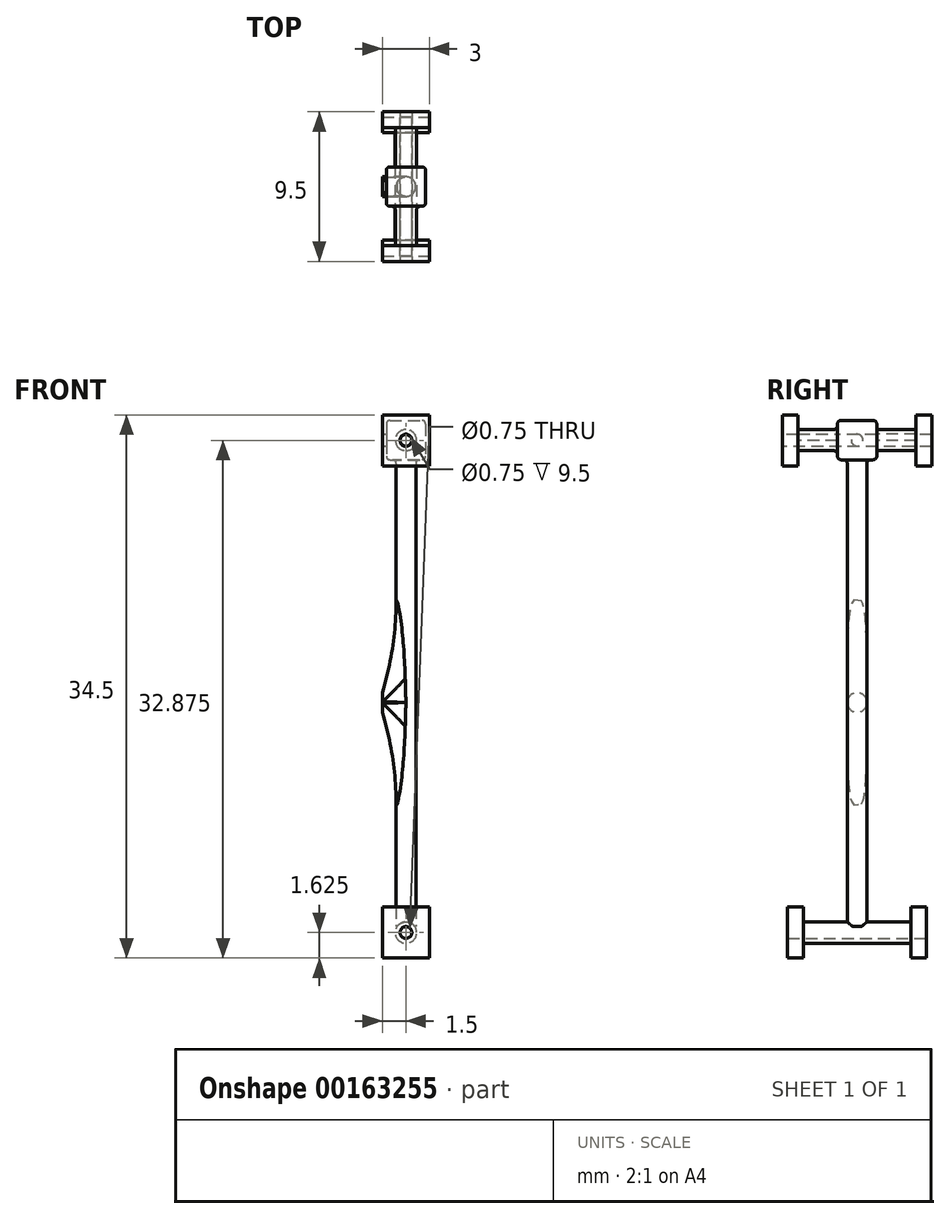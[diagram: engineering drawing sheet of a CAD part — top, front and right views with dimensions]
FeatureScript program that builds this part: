
annotation { "Feature Type Name" : "Feature", "Feature Type Description" : "" }
export const myFeature = defineFeature(function(context is Context, id is Id, definition is map)
    precondition{}
    {
        {
            var Q0;
            Q0=qCreatedBy(makeId("Front.planeOp"),FACE);
            var sketch = newSketch(context, id + "F0", { "sketchPlane" : qUnion([Q0])});
            skLineSegment(sketch, "E0.bottom", {"start": v(0, 0) * mm, "end": v(3, 0) * mm});
            skLineSegment(sketch, "E0.top", {"start": v(0, -3.25) * mm, "end": v(3, -3.25) * mm});
            skLineSegment(sketch, "E0.left", {"start": v(0, 0) * mm, "end": v(0, -3.25) * mm});
            skLineSegment(sketch, "E0.right", {"start": v(3, 0) * mm, "end": v(3, -3.25) * mm});
            skSolve(sketch);
        }
        {
            var Q0;
            Q0 = qSketchRegion(id + "F0", true);
            extrude(context, id + "F1", {"entities" : qUnion([Q0]), "depth" : 1 * mm});
        }
        {
            var Q0;
            Q0=makeQuery(id+"F1.opExtrude","CAP_FACE",FACE,{"disambiguationData":[OSD([sQuery(id+"F0.wireOp",EDGE,"E0.bottom"),sQuery(id+"F0.wireOp",EDGE,"E0.top"),sQuery(id+"F0.wireOp",EDGE,"E0.left"),sQuery(id+"F0.wireOp",EDGE,"E0.right")])],"isStart":true});
            var sketch = newSketch(context, id + "F2", { "sketchPlane" : qUnion([Q0])});
            skCircle(sketch, "E1", {"center": v(-1.5, -1.63) * mm, "radius": 0.38 * mm});
            skPoint(sketch, "E1.centerSnap0", {"position": v(0, -1.63) * mm});
            skPoint(sketch, "E1.centerSnap1", {"position": v(-1.5, 0) * mm});
            skSolve(sketch);
        }
        {
            var Q0;
            Q0 = qSketchRegion(id + "F2", true);
            extrude(context, id + "F3", {"entities" : qUnion([Q0]), "operationType" : NewBodyOperationType.REMOVE, "endBound" : BoundingType.THROUGH_ALL, "oppositeDirection" : true, "depth" : 25 * mm});
        }
        {
            var Q0;
            Q0=makeQuery(id+"F1.opExtrude","CAP_FACE",FACE,{"disambiguationData":[OSD([sQuery(id+"F0.wireOp",EDGE,"E0.bottom"),sQuery(id+"F0.wireOp",EDGE,"E0.top"),sQuery(id+"F0.wireOp",EDGE,"E0.left"),sQuery(id+"F0.wireOp",EDGE,"E0.right")])],"isStart":true});
            var sketch = newSketch(context, id + "F4", { "sketchPlane" : qUnion([Q0])});
            skCircle(sketch, "E2", {"center": v(-1.5, -1.63) * mm, "radius": 0.38 * mm});
            skCircle(sketch, "E3", {"center": v(-1.5, -1.63) * mm, "radius": 0.68 * mm});
            skSolve(sketch);
        }
        {
            var Q0;
            Q0 = qSketchRegion(id + "F4", true);
            extrude(context, id + "F5", {"entities" : qUnion([Q0]), "operationType" : NewBodyOperationType.ADD, "depth" : ((8.83 / 2) - 1) * mm});
        }
        {
            var Q0;
            Q0=makeQuery(id+"F1.opExtrude","SWEPT_BODY",BODY,{"disambiguationData":[OSD([sQuery(id+"F0.wireOp",EDGE,"E0.bottom"),sQuery(id+"F0.wireOp",EDGE,"E0.top"),sQuery(id+"F0.wireOp",EDGE,"E0.left"),sQuery(id+"F0.wireOp",EDGE,"E0.right")])]});
            var Q1;
            Q1=makeQuery(id+"F5.opExtrude","CAP_FACE",FACE,{"disambiguationData":[OSD([sQuery(id+"F4.wireOp",EDGE,"E2"),sQuery(id+"F4.wireOp",EDGE,"E3")])],"isStart":false});
            mirror(context, id + "F6", {"operationType" : NewBodyOperationType.ADD, "entities" : qUnion([Q0]), "mirrorPlane" : qUnion([Q1])});
        }
        {
            var Q0;
            Q0=makeQuery(id+"F1.opExtrude","SWEPT_FACE",FACE,{"disambiguationData":[OSD([sQuery(id+"F0.wireOp",EDGE,"E0.bottom")])]});
            var sketch = newSketch(context, id + "F7", { "sketchPlane" : qUnion([Q0])});
            skCircle(sketch, "E4", {"center": v(1.5, 3.41) * mm, "radius": 0.62 * mm});
            skSolve(sketch);
        }
        {
            var Q0;
            Q0 = qSketchRegion(id + "F7", true);
            extrude(context, id + "F8", {"entities" : qUnion([Q0]), "operationType" : NewBodyOperationType.ADD, "depth" : 29.65 * mm, "hasSecondDirection" : true, "secondDirectionOppositeDirection" : true, "secondDirectionDepth" : 1.25 * mm});
        }
        {
            var Q0;
            Q0=makeQuery(id+"F1.opExtrude","SWEPT_FACE",FACE,{"disambiguationData":[OSD([sQuery(id+"F0.wireOp",EDGE,"E0.left")])]});
            var sketch = newSketch(context, id + "F9", { "sketchPlane" : qUnion([Q0])});
            skCircle(sketch, "E5", {"center": v(-3.41, 12.98) * mm, "radius": 0.62 * mm});
            skSolve(sketch);
        }
        {
            var Q0;
            Q0 = qSketchRegion(id + "F9", true);
            extrude(context, id + "F10", {"entities" : qUnion([Q0]), "operationType" : NewBodyOperationType.ADD, "oppositeDirection" : true, "depth" : 1.5 * mm});
        }
        {
            var Q0;
            {var subQ0=makeQuery(id+"F5.opExtrude","SWEPT_FACE",FACE,{"disambiguationData":[OSD([sQuery(id+"F4.wireOp",EDGE,"E3")])]});var subQ1=sQuery(id+"F7.wireOp",EDGE,"E4");Q0=makeQuery(id+"F10.boolean.opBoolean","INTERSECT",EDGE,{"disambiguationData":[OD(1.0)],"derivedFrom":[makeQuery(id+"F8.boolean.opBoolean","SPLIT",FACE,{"disambiguationData":[TD([subQ0,makeQuery(id+"F6.opPattern","COPY",FACE,{"derivedFrom":subQ0,"instanceName":"1"}),makeQuery(id+"F8.opExtrude","CAP_FACE",FACE,{"disambiguationData":[OSD([subQ1])],"isStart":false})])],"derivedFrom":makeQuery(id+"F8.opExtrude","SWEPT_FACE",FACE,{"disambiguationData":[OSD([subQ1])]})}),makeQuery(id+"F10.opExtrude","SWEPT_FACE",FACE,{"disambiguationData":[OSD([sQuery(id+"F9.wireOp",EDGE,"E5")])]})]});}
            var Q1;
            {var subQ0=makeQuery(id+"F5.opExtrude","SWEPT_FACE",FACE,{"disambiguationData":[OSD([sQuery(id+"F4.wireOp",EDGE,"E3")])]});var subQ1=sQuery(id+"F7.wireOp",EDGE,"E4");Q1=makeQuery(id+"F10.boolean.opBoolean","INTERSECT",EDGE,{"disambiguationData":[OD(0.0)],"derivedFrom":[makeQuery(id+"F8.boolean.opBoolean","SPLIT",FACE,{"disambiguationData":[TD([subQ0,makeQuery(id+"F6.opPattern","COPY",FACE,{"derivedFrom":subQ0,"instanceName":"1"}),makeQuery(id+"F8.opExtrude","CAP_FACE",FACE,{"disambiguationData":[OSD([subQ1])],"isStart":false})])],"derivedFrom":makeQuery(id+"F8.opExtrude","SWEPT_FACE",FACE,{"disambiguationData":[OSD([subQ1])]})}),makeQuery(id+"F10.opExtrude","SWEPT_FACE",FACE,{"disambiguationData":[OSD([sQuery(id+"F9.wireOp",EDGE,"E5")])]})]});}
            fillet(context, id + "F11", {"entities" : qUnion([Q0, Q1]), "radius" : 20 * mm, "tangentPropagation" : true, "allowEdgeOverflow" : false});
        }
        {
            var Q0;
            Q0=makeQuery(id+"F8.opExtrude","CAP_FACE",FACE,{"disambiguationData":[OSD([sQuery(id+"F7.wireOp",EDGE,"E4")])],"isStart":false});
            var sketch = newSketch(context, id + "F12", { "sketchPlane" : qUnion([Q0])});
            skLineSegment(sketch, "E6.bottom", {"start": v(0.25, 2.16) * mm, "end": v(2.75, 2.16) * mm});
            skLineSegment(sketch, "E6.top", {"start": v(0.25, 4.66) * mm, "end": v(2.75, 4.66) * mm});
            skLineSegment(sketch, "E6.left", {"start": v(0.25, 2.16) * mm, "end": v(0.25, 4.66) * mm});
            skLineSegment(sketch, "E6.right", {"start": v(2.75, 2.16) * mm, "end": v(2.75, 4.66) * mm});
            skSolve(sketch);
        }
        {
            var Q0;
            Q0 = qSketchRegion(id + "F12", true);
            extrude(context, id + "F13", {"entities" : qUnion([Q0]), "operationType" : NewBodyOperationType.ADD, "endBound" : BoundingType.SYMMETRIC, "depth" : 2.5 * mm});
        }
        {
            var Q0;
            Q0=makeQuery(id+"F13.opExtrude","SWEPT_FACE",FACE,{"disambiguationData":[OSD([sQuery(id+"F12.wireOp",EDGE,"E6.top")])]});
            var sketch = newSketch(context, id + "F14", { "sketchPlane" : qUnion([Q0])});
            skCircle(sketch, "E7", {"center": v(-1.5, 29.65) * mm, "radius": 0.38 * mm});
            skPoint(sketch, "E7.centerSnap0", {"position": v(-0.25, 29.65) * mm});
            skPoint(sketch, "E7.centerSnap1", {"position": v(-1.5, 30.9) * mm});
            skCircle(sketch, "E8", {"center": v(-1.5, 29.65) * mm, "radius": 0.68 * mm});
            skSolve(sketch);
        }
        {
            var Q0;
            Q0 = qSketchRegion(id + "F14", true);
            extrude(context, id + "F15", {"entities" : qUnion([Q0]), "operationType" : NewBodyOperationType.ADD, "depth" : 2.5 * mm});
        }
        {
            var Q0;
            Q0=makeQuery(id+"F13.opExtrude","SWEPT_FACE",FACE,{"disambiguationData":[OSD([sQuery(id+"F12.wireOp",EDGE,"E6.bottom")])]});
            var sketch = newSketch(context, id + "F16", { "sketchPlane" : qUnion([Q0])});
            skCircle(sketch, "E9", {"center": v(1.5, 29.65) * mm, "radius": 0.38 * mm});
            skPoint(sketch, "E9.centerSnap0", {"position": v(0.25, 29.65) * mm});
            skPoint(sketch, "E9.centerSnap1", {"position": v(1.5, 28.4) * mm});
            skCircle(sketch, "E10", {"center": v(1.5, 29.65) * mm, "radius": 0.68 * mm});
            skSolve(sketch);
        }
        {
            var Q0;
            Q0 = qSketchRegion(id + "F16", true);
            extrude(context, id + "F17", {"entities" : qUnion([Q0]), "operationType" : NewBodyOperationType.ADD, "depth" : 2.5 * mm});
        }
        {
            var Q0;
            Q0=makeQuery(id+"F15.opExtrude","CAP_FACE",FACE,{"disambiguationData":[OSD([sQuery(id+"F14.wireOp",EDGE,"E7"),sQuery(id+"F14.wireOp",EDGE,"E8")])],"isStart":false});
            var sketch = newSketch(context, id + "F18", { "sketchPlane" : qUnion([Q0])});
            skLineSegment(sketch, "E11.bottom", {"start": v(0, 31.25) * mm, "end": v(-3, 31.25) * mm});
            skLineSegment(sketch, "E11.top", {"start": v(0, 28) * mm, "end": v(-3, 28) * mm});
            skLineSegment(sketch, "E11.left", {"start": v(0, 31.25) * mm, "end": v(0, 28) * mm});
            skLineSegment(sketch, "E11.right", {"start": v(-3, 31.25) * mm, "end": v(-3, 28) * mm});
            skSolve(sketch);
        }
        {
            var Q0;
            Q0 = qSketchRegion(id + "F18", true);
            extrude(context, id + "F19", {"entities" : qUnion([Q0]), "operationType" : NewBodyOperationType.ADD, "depth" : 1 * mm});
        }
        {
            var Q0;
            Q0=makeQuery(id+"F17.opExtrude","CAP_FACE",FACE,{"disambiguationData":[OSD([sQuery(id+"F16.wireOp",EDGE,"E9"),sQuery(id+"F16.wireOp",EDGE,"E10")])],"isStart":false});
            var sketch = newSketch(context, id + "F20", { "sketchPlane" : qUnion([Q0])});
            skLineSegment(sketch, "E12.bottom", {"start": v(0, 28) * mm, "end": v(3, 28) * mm});
            skLineSegment(sketch, "E12.top", {"start": v(0, 31.25) * mm, "end": v(3, 31.25) * mm});
            skLineSegment(sketch, "E12.left", {"start": v(0, 28) * mm, "end": v(0, 31.25) * mm});
            skLineSegment(sketch, "E12.right", {"start": v(3, 28) * mm, "end": v(3, 31.25) * mm});
            skSolve(sketch);
        }
        {
            var Q0;
            Q0 = qSketchRegion(id + "F20", true);
            extrude(context, id + "F21", {"entities" : qUnion([Q0]), "operationType" : NewBodyOperationType.ADD, "depth" : 1 * mm});
        }
        {
            var Q0;
            Q0=makeQuery(id+"F21.opExtrude","CAP_FACE",FACE,{"disambiguationData":[OSD([sQuery(id+"F20.wireOp",EDGE,"E12.bottom"),sQuery(id+"F20.wireOp",EDGE,"E12.top"),sQuery(id+"F20.wireOp",EDGE,"E12.left"),sQuery(id+"F20.wireOp",EDGE,"E12.right")])],"isStart":false});
            var sketch = newSketch(context, id + "F22", { "sketchPlane" : qUnion([Q0])});
            skCircle(sketch, "E13", {"center": v(1.5, 29.62) * mm, "radius": 0.38 * mm});
            skPoint(sketch, "E13.centerSnap0", {"position": v(1.5, 28) * mm});
            skPoint(sketch, "E13.centerSnap1", {"position": v(0, 29.62) * mm});
            skSolve(sketch);
        }
        {
            var Q0;
            Q0 = qSketchRegion(id + "F22", true);
            extrude(context, id + "F23", {"entities" : qUnion([Q0]), "operationType" : NewBodyOperationType.REMOVE, "endBound" : BoundingType.THROUGH_ALL, "oppositeDirection" : true, "depth" : 25 * mm});
        }
        {
            var Q0;
            Q0=makeQuery(id+"F13.opExtrude","SWEPT_FACE",FACE,{"disambiguationData":[OSD([sQuery(id+"F12.wireOp",EDGE,"E6.left")])]});
            var Q1;
            Q1=makeQuery(id+"F13.opExtrude","CAP_FACE",FACE,{"disambiguationData":[OSD([sQuery(id+"F12.wireOp",EDGE,"E6.bottom"),sQuery(id+"F12.wireOp",EDGE,"E6.top"),sQuery(id+"F12.wireOp",EDGE,"E6.left"),sQuery(id+"F12.wireOp",EDGE,"E6.right")])],"isStart":false});
            var Q2;
            Q2=makeQuery(id+"F13.opExtrude","SWEPT_FACE",FACE,{"disambiguationData":[OSD([sQuery(id+"F12.wireOp",EDGE,"E6.right")])]});
            var Q3;
            Q3=makeQuery(id+"F13.opExtrude","CAP_FACE",FACE,{"disambiguationData":[OSD([sQuery(id+"F12.wireOp",EDGE,"E6.bottom"),sQuery(id+"F12.wireOp",EDGE,"E6.top"),sQuery(id+"F12.wireOp",EDGE,"E6.left"),sQuery(id+"F12.wireOp",EDGE,"E6.right")])],"isStart":true});
            var Q4;
            {var subQ1=sQuery(id+"F12.wireOp",EDGE,"E6.left");var subQ3=sQuery(id+"F12.wireOp",EDGE,"E6.bottom");Q4=makeQuery(id+"F17.boolean.opBoolean","SPLIT",FACE,{"disambiguationData":[TD([makeQuery(id+"F13.opExtrude","SWEPT_FACE",FACE,{"disambiguationData":[OSD([subQ1])]})])],"derivedFrom":makeQuery(id+"F13.opExtrude","SWEPT_FACE",FACE,{"disambiguationData":[OSD([subQ3])]})});}
            var Q5;
            Q5=makeQuery(id+"F15.opExtrude","CAP_EDGE",EDGE,{"disambiguationData":[OSD([sQuery(id+"F14.wireOp",EDGE,"E8")])],"isStart":true});
            fillet(context, id + "F24", {"entities" : qUnion([Q0, Q1, Q2, Q3, Q4, Q5]), "radius" : .23 * mm, "tangentPropagation" : true, "allowEdgeOverflow" : false});
        }
        {
            var Q0;
            Q0=makeQuery(id+"F13.opExtrude","SWEPT_FACE",FACE,{"disambiguationData":[OSD([sQuery(id+"F12.wireOp",EDGE,"E6.left")])]});
            var sketch = newSketch(context, id + "F25", { "sketchPlane" : qUnion([Q0])});
            skCircle(sketch, "E14", {"center": v(-3.41, 29.65) * mm, "radius": 0.38 * mm});
            skPoint(sketch, "E14.centerSnap0", {"position": v(-3.41, 30.67) * mm});
            skPoint(sketch, "E14.centerSnap1", {"position": v(-4.43, 29.65) * mm});
            skSolve(sketch);
        }
        {
            var Q0;
            Q0 = qSketchRegion(id + "F25", true);
            extrude(context, id + "F26", {"entities" : qUnion([Q0]), "operationType" : NewBodyOperationType.ADD, "depth" : .25 * mm});
        }
    });
